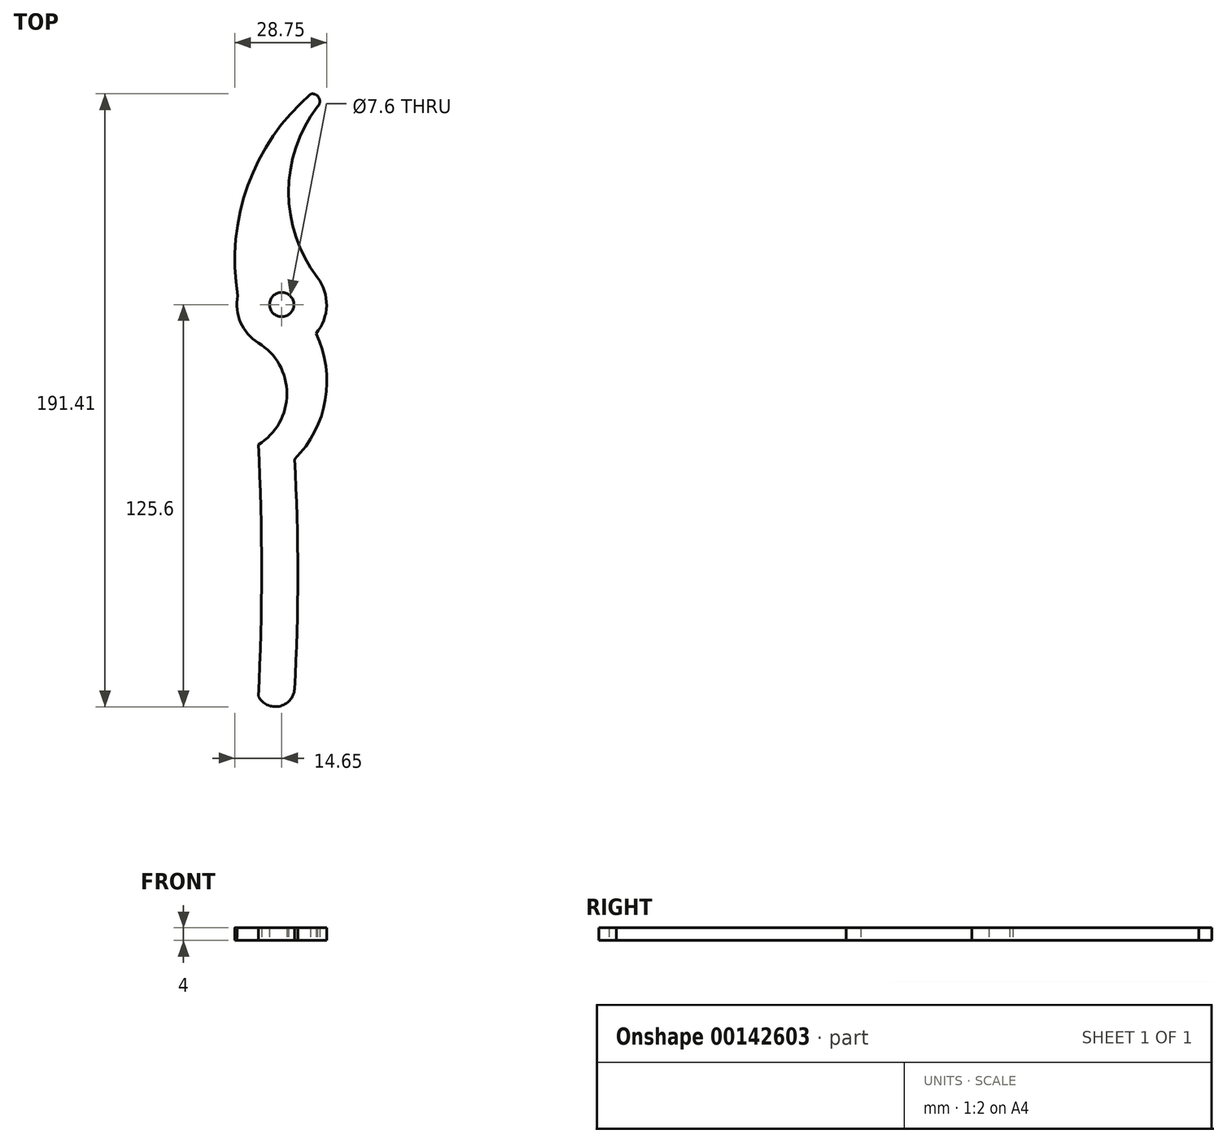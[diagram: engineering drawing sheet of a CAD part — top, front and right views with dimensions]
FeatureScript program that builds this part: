
annotation { "Feature Type Name" : "Feature", "Feature Type Description" : "" }
export const myFeature = defineFeature(function(context is Context, id is Id, definition is map)
    precondition{}
    {
        {
            var Q0;
            Q0=qCreatedBy(makeId("Top.planeOp"),FACE);
            var sketch = newSketch(context, id + "F0", { "sketchPlane" : qUnion([Q0])});
            skCircle(sketch, "E0", {"center": v(0, 0) * mm, "radius": 3.8 * mm});
            skCircle(sketch, "E1", {"center": v(0, 0) * mm, "radius": 14 * mm});
            skArc(sketch, "E2", {"start": v(0, -14) * mm, "mid": v(12.54, -6.22) * mm, "end": v(11.14, 8.48) * mm});
            skArc(sketch, "E3", {"start": v(-7.3, -43.75) * mm, "mid": v(1.62, -27.85) * mm, "end": v(-7.3, -11.95) * mm});
            skArc(sketch, "E4", {"start": v(4.01, -48.32) * mm, "mid": v(13.6, -29.74) * mm, "end": v(10.7, -9.02) * mm});
            skArc(sketch, "E5", {"start": v(-7.3, -122.35) * mm, "mid": v(-6.3, -83.05) * mm, "end": v(-7.3, -43.75) * mm});
            skArc(sketch, "E6", {"start": v(4.01, -120.12) * mm, "mid": v(5.02, -84.22) * mm, "end": v(4.01, -48.32) * mm});
            skArc(sketch, "E7", {"start": v(-7.3, -122.35) * mm, "mid": v(-0.8, -125.48) * mm, "end": v(4.01, -120.12) * mm});
            skArc(sketch, "E8", {"start": v(11.14, 61.78) * mm, "mid": v(2.15, 35.13) * mm, "end": v(11.14, 8.48) * mm});
            skArc(sketch, "E9", {"start": v(9.03, 65.75) * mm, "mid": v(-10.58, 37.22) * mm, "end": v(-13.73, 2.75) * mm});
            skArc(sketch, "E10", {"start": v(11.14, 61.78) * mm, "mid": v(11.6, 64.58) * mm, "end": v(9.03, 65.75) * mm});
            skSolve(sketch);
        }
        {
            var Q0;
            {var subQ0=sQuery(id+"F0.wireOp",EDGE,"Zl2vqRVg-j4ew-T5TA-GzTa-eQ3nDUfPPO8E");Q0=makeQuery(id+"F0.imprint","IMPRINT",FACE,{"disambiguationData":[TD([[makeQuery(id+"F0.imprint","IMPRINT",EDGE,{"derivedFrom":subQ0}),-1.0]])]});}
            var Q1;
            Q1=makeQuery(id+"F0.imprint","IMPRINT",FACE,{"disambiguationData":[TD([[makeQuery(id+"F0.imprint","IMPRINT",EDGE,{"derivedFrom":sQuery(id+"F0.wireOp",EDGE,"E0")}),-1.0]])]});
            var Q2;
            {var subQ1=sQuery(id+"F0.wireOp",EDGE,"E3");Q2=makeQuery(id+"F0.imprint","IMPRINT",FACE,{"disambiguationData":[TD([[makeQuery(id+"F0.imprint","IMPRINT",EDGE,{"derivedFrom":subQ1}),-1.0]])]});}
            var Q3;
            {var subQ0=sQuery(id+"F0.wireOp",EDGE,"E8");Q3=makeQuery(id+"F0.imprint","IMPRINT",FACE,{"disambiguationData":[TD([[makeQuery(id+"F0.imprint","IMPRINT",EDGE,{"derivedFrom":subQ0}),-1.0]])]});}
            extrude(context, id + "F1", {"entities" : qUnion([Q0, Q1, Q2, Q3]), "depth" : 4 * mm});
        }
    });
